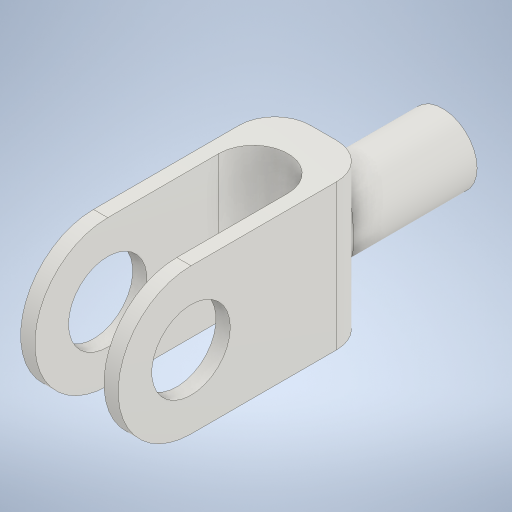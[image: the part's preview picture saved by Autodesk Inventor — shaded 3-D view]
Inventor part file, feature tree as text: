
AUTODESK INVENTOR PART (.ipt)
format: ipt  version: 2024 (Build 280153000, 153)  size: 324,608 bytes
history: native  units: mm
features: extrude x4, sketch x4, other x3, fillet x2
ambient origin geometry x8: Origin, YZ Plane, XZ Plane, XY Plane, X Axis, Y Axis, Z Axis, Center Point
bodies: Solid1 (feature_tree)
feature tree (13):
  extrude  "Extrusion1"  Depth=33.0mm
  extrude  "Extrusion2"  Depth=66.0mm
  extrude  "Extrusion3"  Depth=50.0mm TaperAngle=0.0deg
  other  "Full Round Fillet1"
  other  "Full Round Fillet2"
  extrude  "Extrusion4"  Depth=2.0mm
  other  "Full Round Fillet3"
  fillet  "Fillet1"  Radius=30.6mm
  fillet  "Fillet2"  Radius=20.5mm
  sketch  "Sketch1"  dims[d0=29.0mm d1=33.0mm]
  sketch  "Sketch2"  dims[d2=52.0mm d3=66.0mm]
  sketch  "Sketch3"  dims[d4=26.0mm d5=50.0mm d6=0.0mm]
  sketch  "Sketch4"  dims[d7=41.0mm d8=61.2mm d9=30.6mm d10=20.5mm d11=15.0mm d12=0.0mm d13=6.0mm d15=6.0mm d16=91.8mm d17=0.0mm d18=33.0mm d19=30.6mm d20=30.6mm d21=50.0mm d22=0.0mm d23=15.0mm d24=2.0mm]
